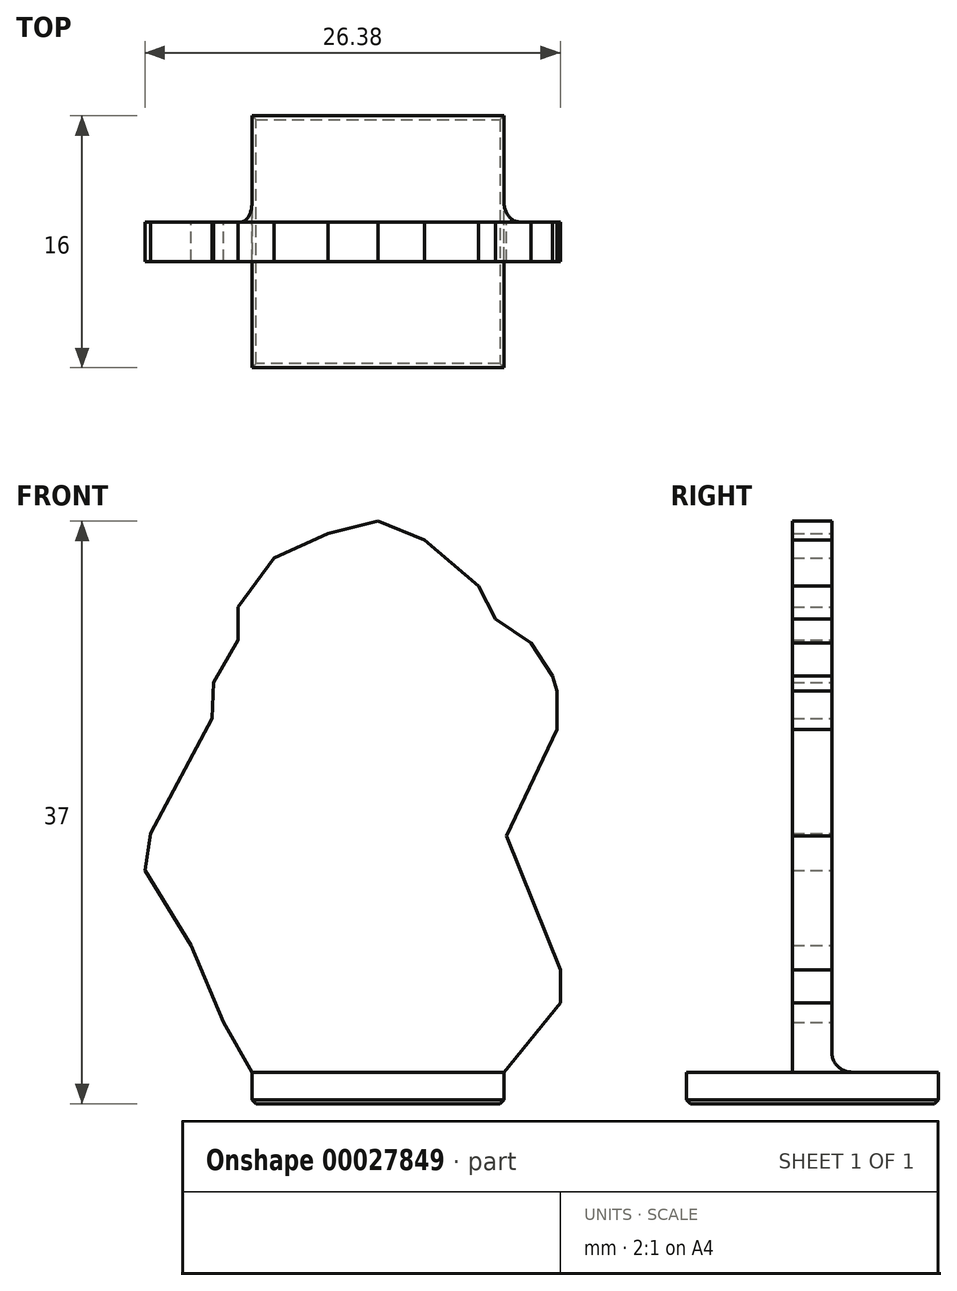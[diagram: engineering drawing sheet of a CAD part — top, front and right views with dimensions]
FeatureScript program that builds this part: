
annotation { "Feature Type Name" : "Feature", "Feature Type Description" : "" }
export const myFeature = defineFeature(function(context is Context, id is Id, definition is map)
    precondition{}
    {
        {
            var Q0;
            Q0=qCreatedBy(makeId("Top.planeOp"),FACE);
            var sketch = newSketch(context, id + "F0", { "sketchPlane" : qUnion([Q0])});
            skLineSegment(sketch, "E0.rect.bottom", {"start": v(8, 8) * mm, "end": v(-8, 8) * mm});
            skLineSegment(sketch, "E0.rect.top", {"start": v(8, -8) * mm, "end": v(-8, -8) * mm});
            skLineSegment(sketch, "E0.rect.left", {"start": v(8, 8) * mm, "end": v(8, -8) * mm});
            skLineSegment(sketch, "E0.rect.right", {"start": v(-8, 8) * mm, "end": v(-8, -8) * mm});
            skPoint(sketch, "E0.rect.middle", {"position": v(0, 0) * mm});
            skSolve(sketch);
        }
        {
            var Q0;
            Q0 = qSketchRegion(id + "F0", true);
            extrude(context, id + "F1", {"entities" : qUnion([Q0]), "depth" : 2 * mm});
        }
        {
            var Q0;
            Q0=qCreatedBy(makeId("Front.planeOp"),FACE);
            var sketch = newSketch(context, id + "F2", { "sketchPlane" : qUnion([Q0])});
            skLineSegment(sketch, "E1", {"start": v(0, 2) * mm, "end": v(0, 37) * mm});
            skPoint(sketch, "E2.0", {"position": v(-8, 2) * mm});
            skPoint(sketch, "E3.0", {"position": v(8, 2) * mm});
            skPoint(sketch, "E4", {"position": v(11.58, 6.4) * mm});
            skPoint(sketch, "E5", {"position": v(11.58, 8.49) * mm});
            skPoint(sketch, "E6", {"position": v(8.16, 17) * mm});
            skPoint(sketch, "E7", {"position": v(11.38, 23.75) * mm});
            skPoint(sketch, "E8", {"position": v(2.96, 35.8) * mm});
            skPoint(sketch, "E9", {"position": v(6.4, 32.9) * mm});
            skPoint(sketch, "E10", {"position": v(9.71, 29.26) * mm});
            skPoint(sketch, "E11", {"position": v(-3.16, 36.22) * mm});
            skPoint(sketch, "E12", {"position": v(-6.6, 34.66) * mm});
            skPoint(sketch, "E13", {"position": v(-8.88, 31.54) * mm});
            skPoint(sketch, "E14", {"position": v(-8.88, 29.47) * mm});
            skPoint(sketch, "E15", {"position": v(-10.43, 26.76) * mm});
            skPoint(sketch, "E16", {"position": v(-14.8, 14.82) * mm});
            skPoint(sketch, "E17", {"position": v(-11.89, 10.04) * mm});
            skPoint(sketch, "E18", {"position": v(-9.81, 5.16) * mm});
            skLineSegment(sketch, "E19", {"start": v(-8, 2) * mm, "end": v(8, 2) * mm});
            skLineSegment(sketch, "E20", {"start": v(8, 2) * mm, "end": v(11.58, 6.4) * mm});
            skLineSegment(sketch, "E21", {"start": v(11.58, 6.4) * mm, "end": v(11.58, 8.49) * mm});
            skLineSegment(sketch, "E22", {"start": v(8.16, 17) * mm, "end": v(11.58, 8.49) * mm});
            skLineSegment(sketch, "E23", {"start": v(8.16, 17) * mm, "end": v(11.38, 23.75) * mm});
            skLineSegment(sketch, "E24", {"start": v(2.96, 35.8) * mm, "end": v(6.4, 32.9) * mm});
            skLineSegment(sketch, "E25", {"start": v(2.96, 35.8) * mm, "end": v(0, 37) * mm});
            skLineSegment(sketch, "E26", {"start": v(-3.16, 36.22) * mm, "end": v(0, 37) * mm});
            skLineSegment(sketch, "E27", {"start": v(-3.16, 36.22) * mm, "end": v(-6.6, 34.66) * mm});
            skLineSegment(sketch, "E28", {"start": v(-6.6, 34.66) * mm, "end": v(-8.88, 31.54) * mm});
            skLineSegment(sketch, "E29", {"start": v(-8.88, 31.54) * mm, "end": v(-8.88, 29.47) * mm});
            skLineSegment(sketch, "E30", {"start": v(-8.88, 29.47) * mm, "end": v(-10.43, 26.76) * mm});
            skLineSegment(sketch, "E31", {"start": v(-14.8, 14.82) * mm, "end": v(-11.89, 10.04) * mm});
            skLineSegment(sketch, "E32", {"start": v(-11.89, 10.04) * mm, "end": v(-9.81, 5.16) * mm});
            skLineSegment(sketch, "E33", {"start": v(-9.81, 5.16) * mm, "end": v(-8, 2) * mm});
            skPoint(sketch, "E34", {"position": v(7.47, 30.78) * mm});
            skLineSegment(sketch, "E35", {"start": v(6.4, 32.9) * mm, "end": v(7.47, 30.78) * mm});
            skLineSegment(sketch, "E36", {"start": v(7.47, 30.78) * mm, "end": v(9.71, 29.26) * mm});
            skPoint(sketch, "E37", {"position": v(-14.44, 17.17) * mm});
            skPoint(sketch, "E38", {"position": v(-10.53, 24.46) * mm});
            skLineSegment(sketch, "E39", {"start": v(-10.43, 26.76) * mm, "end": v(-10.53, 24.46) * mm});
            skLineSegment(sketch, "E40", {"start": v(-10.53, 24.46) * mm, "end": v(-14.44, 17.17) * mm});
            skLineSegment(sketch, "E41", {"start": v(-14.44, 17.17) * mm, "end": v(-14.8, 14.82) * mm});
            skPoint(sketch, "E42", {"position": v(11.07, 27.16) * mm});
            skPoint(sketch, "E43", {"position": v(11.38, 26.2) * mm});
            skLineSegment(sketch, "E44", {"start": v(9.71, 29.26) * mm, "end": v(11.07, 27.16) * mm});
            skLineSegment(sketch, "E45", {"start": v(11.38, 26.2) * mm, "end": v(11.38, 23.75) * mm});
            skLineSegment(sketch, "E46", {"start": v(11.38, 26.2) * mm, "end": v(11.07, 27.16) * mm});
            skSolve(sketch);
        }
        {
            var Q0;
            Q0 = qSketchRegion(id + "F2", true);
            extrude(context, id + "F3", {"entities" : qUnion([Q0]), "operationType" : NewBodyOperationType.ADD, "depth" : 1.25 * mm, "hasSecondDirection" : true, "secondDirectionOppositeDirection" : true, "secondDirectionDepth" : 1.25 * mm});
        }
        {
            var Q0;
            Q0=makeQuery(id+"F3.opExtrude","CAP_EDGE",EDGE,{"disambiguationData":[OSD([sQuery(id+"F2.wireOp",EDGE,"E19")])],"isStart":false});
            var Q1;
            Q1=makeQuery(id+"F3.opExtrude","CAP_EDGE",EDGE,{"disambiguationData":[OSD([sQuery(id+"F2.wireOp",EDGE,"E19")])],"isStart":true});
            fillet(context, id + "F4", {"entities" : qUnion([Q0, Q1]), "radius" : 1.25 * mm, "tangentPropagation" : true, "allowEdgeOverflow" : false});
        }
        {
            var Q0;
            Q0=makeQuery(id+"F1.opExtrude","CAP_EDGE",EDGE,{"disambiguationData":[OSD([sQuery(id+"F0.wireOp",EDGE,"E0.rect.top")])],"isStart":true});
            var Q1;
            Q1=makeQuery(id+"F1.opExtrude","CAP_EDGE",EDGE,{"disambiguationData":[OSD([sQuery(id+"F0.wireOp",EDGE,"E0.rect.left")])],"isStart":true});
            var Q2;
            Q2=makeQuery(id+"F1.opExtrude","CAP_EDGE",EDGE,{"disambiguationData":[OSD([sQuery(id+"F0.wireOp",EDGE,"E0.rect.bottom")])],"isStart":true});
            var Q3;
            Q3=makeQuery(id+"F1.opExtrude","CAP_EDGE",EDGE,{"disambiguationData":[OSD([sQuery(id+"F0.wireOp",EDGE,"E0.rect.right")])],"isStart":true});
            chamfer(context, id + "F5", {"entities" : qUnion([Q0, Q1, Q2, Q3]), "width" : .25 * mm, "tangentPropagation" : true});
        }
    });
